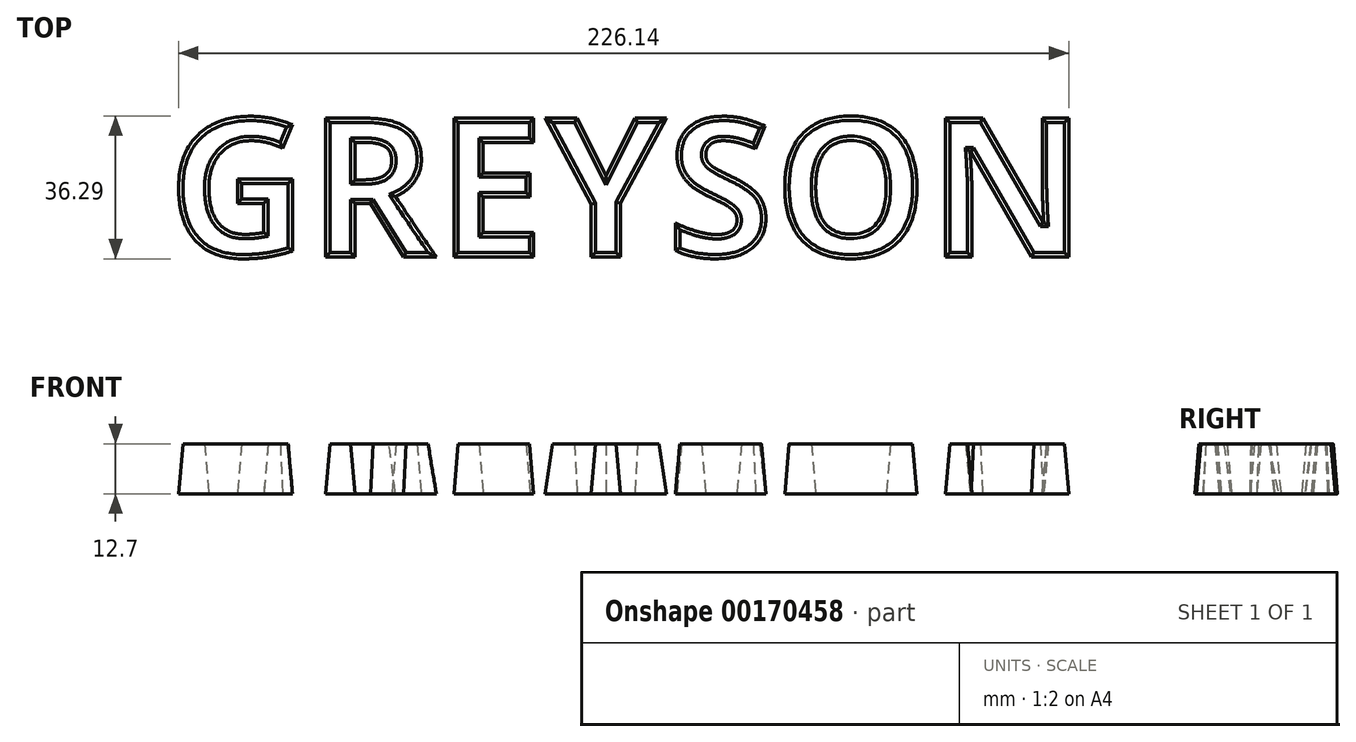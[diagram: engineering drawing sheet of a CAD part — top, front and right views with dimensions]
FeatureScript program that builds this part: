
annotation { "Feature Type Name" : "Feature", "Feature Type Description" : "" }
export const myFeature = defineFeature(function(context is Context, id is Id, definition is map)
    precondition{}
    {
        {
            var Q0;
            Q0=qCreatedBy(makeId("Top.planeOp"),FACE);
            var sketch = newSketch(context, id + "F0", { "sketchPlane" : qUnion([Q0])});
            skText(sketch, "E0", { "text": "GREYSON", "fontName": "OpenSans-Bold.ttf"});
            const initialGuessF0  = {"E0": [-0.08304, 0, 1, 0, 0.03555]};
            skSetInitialGuess(sketch, initialGuessF0);
            skSolve(sketch);
        }
        {
            var Q0;
            Q0 = qSketchRegion(id + "F0", true);
            var Q1;
            Q1 = qConstructionFilter(qBodyType(qCreatedBy(id + "F0" ,EDGE), BodyType.WIRE), ConstructionObject.NO);
            extrude(context, id + "F1", {"entities" : qUnion([Q0]), "surfaceEntities" : qUnion([Q1]), "depth" : 12.7 * mm, "offsetDistance" : 25.4 * mm, "hasDraft" : true, "draftAngle" : 5 * degree, "draftPullDirection" : true});
        }
    });
